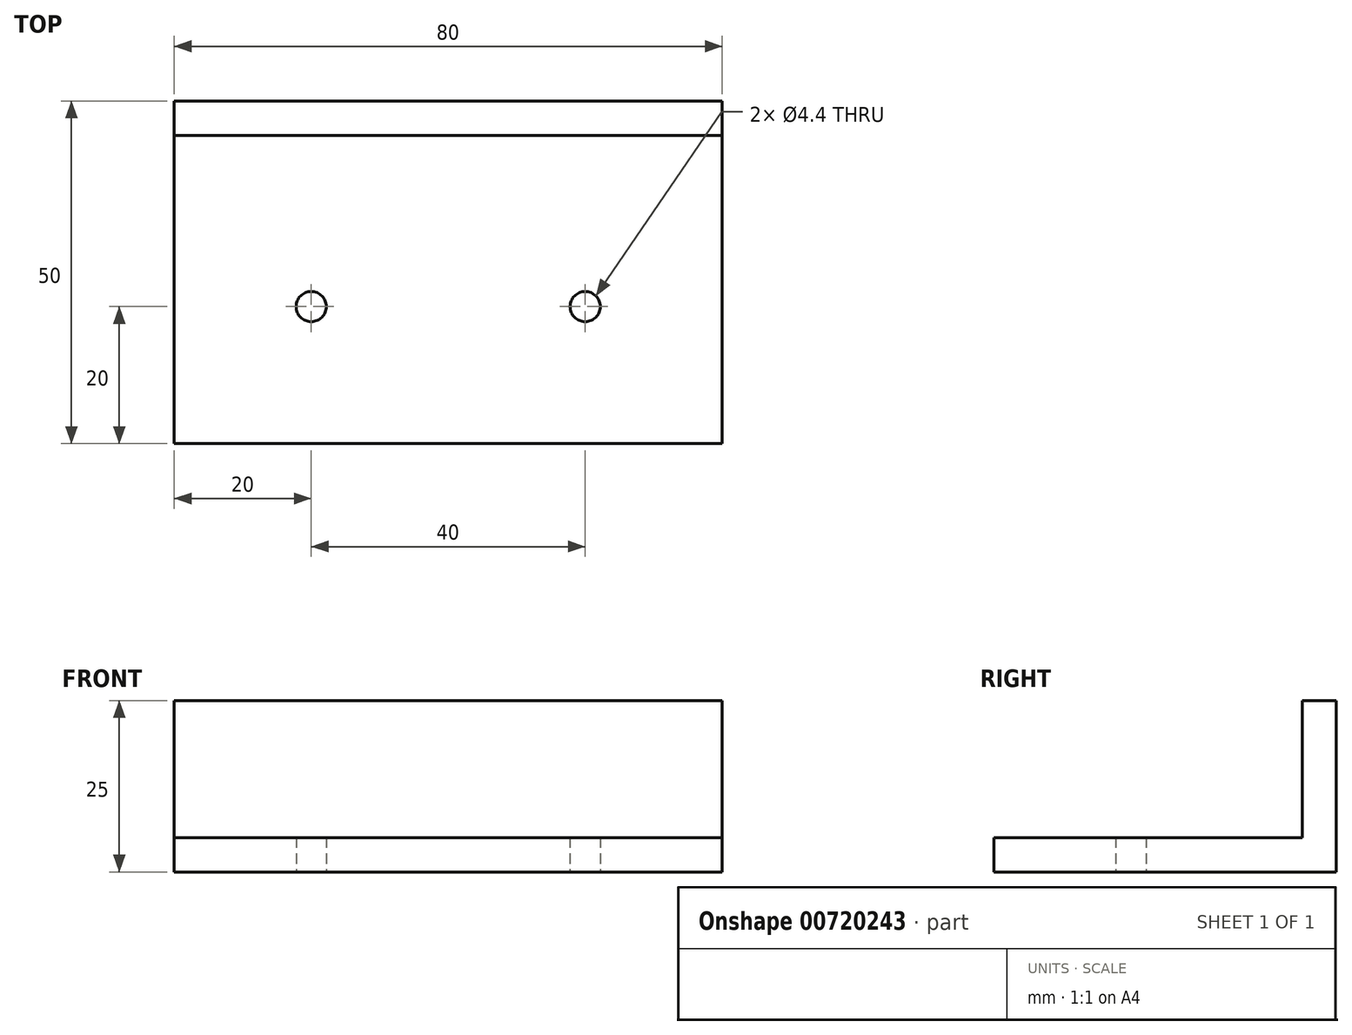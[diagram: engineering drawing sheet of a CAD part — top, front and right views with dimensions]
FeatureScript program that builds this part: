
annotation { "Feature Type Name" : "Feature", "Feature Type Description" : "" }
export const myFeature = defineFeature(function(context is Context, id is Id, definition is map)
    precondition{}
    {
        {
            var Q0;
            Q0=qCreatedBy(makeId("Top.planeOp"),FACE);
            var sketch = newSketch(context, id + "F0", { "sketchPlane" : qUnion([Q0])});
            skLineSegment(sketch, "E0.bottom", {"start": v(40, 25) * mm, "end": v(-40, 25) * mm});
            skLineSegment(sketch, "E0.top", {"start": v(40, -25) * mm, "end": v(-40, -25) * mm});
            skLineSegment(sketch, "E0.left", {"start": v(40, 25) * mm, "end": v(40, -25) * mm});
            skLineSegment(sketch, "E0.right", {"start": v(-40, 25) * mm, "end": v(-40, -25) * mm});
            skPoint(sketch, "E0.middle", {"position": v(0, 0) * mm});
            skSolve(sketch);
        }
        {
            var Q0;
            Q0 = qSketchRegion(id + "F0", true);
            extrude(context, id + "F1", {"entities" : qUnion([Q0]), "depth" : 5 * mm, "offsetDistance" : 25 * mm});
        }
        {
            var Q0;
            Q0=makeQuery(id+"F1.opExtrude","CAP_FACE",FACE,{"disambiguationData":[OSD([sQuery(id+"F0.wireOp",EDGE,"E0.bottom"),sQuery(id+"F0.wireOp",EDGE,"E0.top"),sQuery(id+"F0.wireOp",EDGE,"E0.left"),sQuery(id+"F0.wireOp",EDGE,"E0.right")])],"isStart":false});
            var sketch = newSketch(context, id + "F2", { "sketchPlane" : qUnion([Q0])});
            skLineSegment(sketch, "E1.bottom", {"start": v(-40, 20) * mm, "end": v(40, 20) * mm});
            skLineSegment(sketch, "E1.top", {"start": v(-40, 10) * mm, "end": v(40, 10) * mm});
            skLineSegment(sketch, "E1.left", {"start": v(-40, 20) * mm, "end": v(-40, 10) * mm});
            skLineSegment(sketch, "E1.right", {"start": v(40, 20) * mm, "end": v(40, 10) * mm});
            skSolve(sketch);
        }
        {
            var Q0;
            Q0=makeQuery(id+"F2.imprint","IMPRINT",FACE,{"disambiguationData":[TD([[makeQuery(id+"F2.imprint","IMPRINT",EDGE,{"derivedFrom":sQuery(id+"F2.wireOp",EDGE,"E1.bottom")}),1.0]])]});
            extrude(context, id + "F3", {"entities" : qUnion([Q0]), "operationType" : NewBodyOperationType.ADD, "depth" : 20 * mm, "offsetDistance" : 25 * mm});
        }
        {
            var Q0;
            Q0=makeQuery(id+"F1.opExtrude","CAP_FACE",FACE,{"disambiguationData":[OSD([sQuery(id+"F0.wireOp",EDGE,"E0.bottom"),sQuery(id+"F0.wireOp",EDGE,"E0.top"),sQuery(id+"F0.wireOp",EDGE,"E0.left"),sQuery(id+"F0.wireOp",EDGE,"E0.right")])],"isStart":false});
            var sketch = newSketch(context, id + "F4", { "sketchPlane" : qUnion([Q0])});
            skPoint(sketch, "E2", {"position": v(-20, -5) * mm});
            skPoint(sketch, "E3", {"position": v(20, -5) * mm});
            skSolve(sketch);
        }
        {
            var Q0;
            Q0=sQuery(id+"F4.wireOp",VERTEX,"E2");
            var Q1;
            Q1=sQuery(id+"F4.wireOp",VERTEX,"E3");
            var Q2;
            Q2=makeQuery(id+"F1.opExtrude","SWEPT_BODY",BODY,{"disambiguationData":[OSD([sQuery(id+"F0.wireOp",EDGE,"E0.bottom"),sQuery(id+"F0.wireOp",EDGE,"E0.top"),sQuery(id+"F0.wireOp",EDGE,"E0.left"),sQuery(id+"F0.wireOp",EDGE,"E0.right")])]});
            hole(context, id + "F5", {"style" : HoleStyle.SIMPLE, "endStyle" : HoleEndStyle.THROUGH, "standardTappedOrClearance" : lookupTablePath({ "fit" : "Normal", "standard" : "ISO", "size" : "M4", "type" : "Clearance" }), "standardBlindInLast" : lookupTablePath({ "fit" : "Standard", "standard" : "ISO", "size" : "M4", "type" : "Clearance" }), "holeDiameter" : 4.4 * mm, "majorDiameter" : 5 * mm, "tappedDepth" : 12 * mm, "tapClearance" : 3, "locations" : qUnion([Q0, Q1]), "scope" : qUnion([Q2])});
        }
    });
